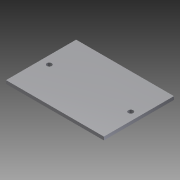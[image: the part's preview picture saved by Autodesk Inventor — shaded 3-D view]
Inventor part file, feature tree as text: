
AUTODESK INVENTOR PART (.ipt)
format: ipt  version: 2012 (Build 160160000, 160)  size: 76,288 bytes
history: native  units: mm
features: extrude x1, sketch x1
ambient origin geometry x8: Origin, YZ Plane, XZ Plane, XY Plane, X Axis, Y Axis, Z Axis, Center Point
bodies: Solid1 (feature_tree)
feature tree (2):
  extrude  "Extrusion1"  Depth=2.0mm TaperAngle=0.0deg
  sketch  "Sketch1"  dims[d0=60.0mm d1=43.0mm d2=3.0mm d3=21.5mm d4=5.0mm d5=3.0mm d6=5.0mm d7=21.5mm d8=2.0mm d9=0.0mm]
